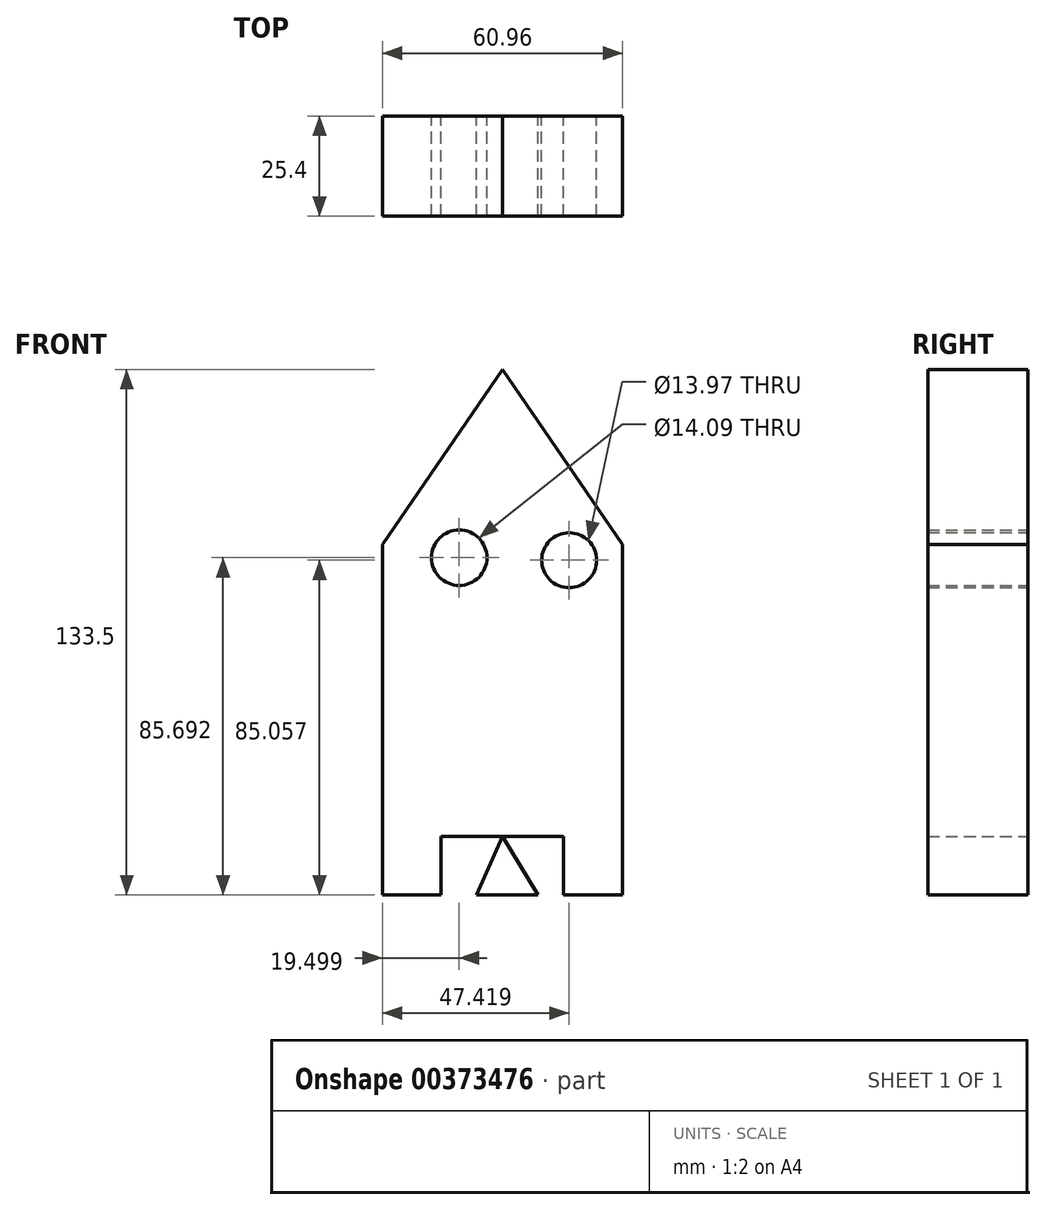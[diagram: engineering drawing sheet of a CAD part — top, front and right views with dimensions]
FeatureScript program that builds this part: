
annotation { "Feature Type Name" : "Feature", "Feature Type Description" : "" }
export const myFeature = defineFeature(function(context is Context, id is Id, definition is map)
    precondition{}
    {
        {
            var Q0;
            Q0=qCreatedBy(makeId("Front.planeOp"),FACE);
            var sketch = newSketch(context, id + "F0", { "sketchPlane" : qUnion([Q0])});
            skLineSegment(sketch, "E0.top", {"start": v(0, -52.88) * mm, "end": v(-60.96, -52.88) * mm});
            skLineSegment(sketch, "E0.left", {"start": v(0, 21.18) * mm, "end": v(0, -52.88) * mm});
            skLineSegment(sketch, "E0.right", {"start": v(-60.96, 21.18) * mm, "end": v(-60.96, -52.88) * mm});
            skLineSegment(sketch, "E1", {"start": v(-60.96, 21.18) * mm, "end": v(-30.48, 65.68) * mm});
            skLineSegment(sketch, "E2", {"start": v(0, 21.18) * mm, "end": v(-30.48, 65.68) * mm});
            skLineSegment(sketch, "E3", {"start": v(-60.96, -7.51) * mm, "end": v(-24.78, -7.51) * mm});
            skLineSegment(sketch, "E4.trimOffspring", {"start": v(-13.94, -7.51) * mm, "end": v(0, -7.51) * mm});
            skLineSegment(sketch, "E5", {"start": v(-30.48, 65.68) * mm, "end": v(-30.48, -7.51) * mm});
            skLineSegment(sketch, "E6", {"start": v(-60.96, -52.88) * mm, "end": v(-54.25, -52.88) * mm});
            skLineSegment(sketch, "E7", {"start": v(-24.78, -7.51) * mm, "end": v(-13.94, -7.51) * mm});
            skLineSegment(sketch, "E8", {"start": v(0, -52.88) * mm, "end": v(0, -67.82) * mm});
            skLineSegment(sketch, "E9", {"start": v(-60.96, -52.88) * mm, "end": v(-60.96, -67.82) * mm});
            skLineSegment(sketch, "E10", {"start": v(-60.96, -67.82) * mm, "end": v(-46.02, -67.82) * mm});
            skLineSegment(sketch, "E11", {"start": v(0, -67.82) * mm, "end": v(-14.94, -67.82) * mm});
            skLineSegment(sketch, "E12", {"start": v(-14.94, -67.82) * mm, "end": v(-14.94, -52.88) * mm});
            skLineSegment(sketch, "E13", {"start": v(-46.02, -67.82) * mm, "end": v(-46.02, -52.88) * mm});
            skCircle(sketch, "E14", {"center": v(-41.46, 17.87) * mm, "radius": 7.04 * mm});
            skCircle(sketch, "E15", {"center": v(-13.54, 17.24) * mm, "radius": 6.99 * mm});
            skPoint(sketch, "E16.start.orphan", {"position": v(-30.48, -52.88) * mm});
            skLineSegment(sketch, "E17", {"start": v(-30.48, -52.88) * mm, "end": v(-37.02, -67.8) * mm});
            skLineSegment(sketch, "E18", {"start": v(-37.02, -67.8) * mm, "end": v(-30.48, -52.88) * mm});
            skLineSegment(sketch, "E19", {"start": v(-21.47, -67.8) * mm, "end": v(-30.48, -52.88) * mm});
            skLineSegment(sketch, "E20", {"start": v(-37.02, -67.8) * mm, "end": v(-21.47, -67.8) * mm});
            skLineSegment(sketch, "E21", {"start": v(-33.75, -60.34) * mm, "end": v(-25.98, -60.34) * mm});
            skLineSegment(sketch, "E22", {"start": v(-35.6, -64.55) * mm, "end": v(-23.43, -64.55) * mm});
            skSolve(sketch);
        }
        {
            var Q0;
            Q0 = qSketchRegion(id + "F0", true);
            extrude(context, id + "F1", {"entities" : qUnion([Q0]), "depth" : 25.4 * mm});
        }
        {
            var Q0;
            Q0 = qSketchRegion(id + "F0", true);
            extrude(context, id + "F2", {"entities" : qUnion([Q0]), "operationType" : NewBodyOperationType.ADD, "depth" : 25.4 * mm});
        }
    });
